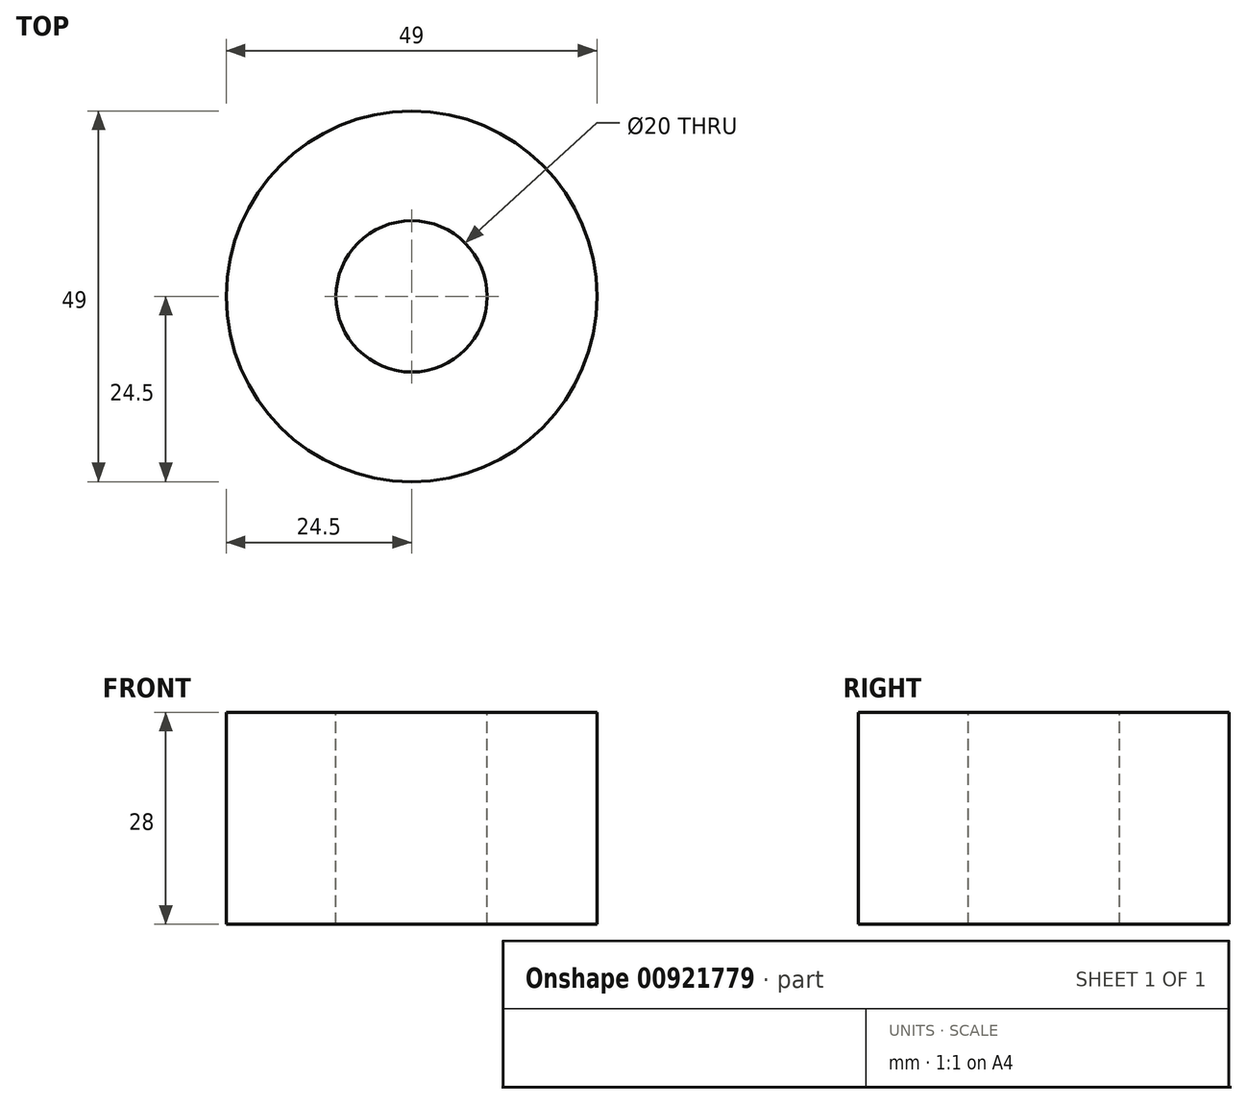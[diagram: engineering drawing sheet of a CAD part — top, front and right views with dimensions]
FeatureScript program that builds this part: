
annotation { "Feature Type Name" : "Feature", "Feature Type Description" : "" }
export const myFeature = defineFeature(function(context is Context, id is Id, definition is map)
    precondition{}
    {
        {
            var Q0;
            Q0=qCreatedBy(makeId("Top.planeOp"),FACE);
            var sketch = newSketch(context, id + "F0", { "sketchPlane" : qUnion([Q0])});
            skCircle(sketch, "E0", {"center": v(0, 0) * mm, "radius": 24.5 * mm});
            skSolve(sketch);
        }
        {
            var Q0;
            Q0 = qSketchRegion(id + "F0", true);
            extrude(context, id + "F1", {"entities" : qUnion([Q0]), "oppositeDirection" : true, "depth" : 28 * mm, "offsetDistance" : 25 * mm});
        }
        {
            var Q0;
            Q0=makeQuery(id+"F1.opExtrude","CAP_FACE",FACE,{"disambiguationData":[OSD([sQuery(id+"F0.wireOp",EDGE,"E0")])],"isStart":true});
            var sketch = newSketch(context, id + "F2", { "sketchPlane" : qUnion([Q0])});
            skCircle(sketch, "E1", {"center": v(0, 0) * mm, "radius": 10 * mm});
            skSolve(sketch);
        }
        {
            var Q0;
            Q0 = qSketchRegion(id + "F2", true);
            extrude(context, id + "F3", {"entities" : qUnion([Q0]), "operationType" : NewBodyOperationType.REMOVE, "endBound" : BoundingType.THROUGH_ALL, "oppositeDirection" : true, "depth" : 25 * mm, "offsetDistance" : 25 * mm});
        }
    });
